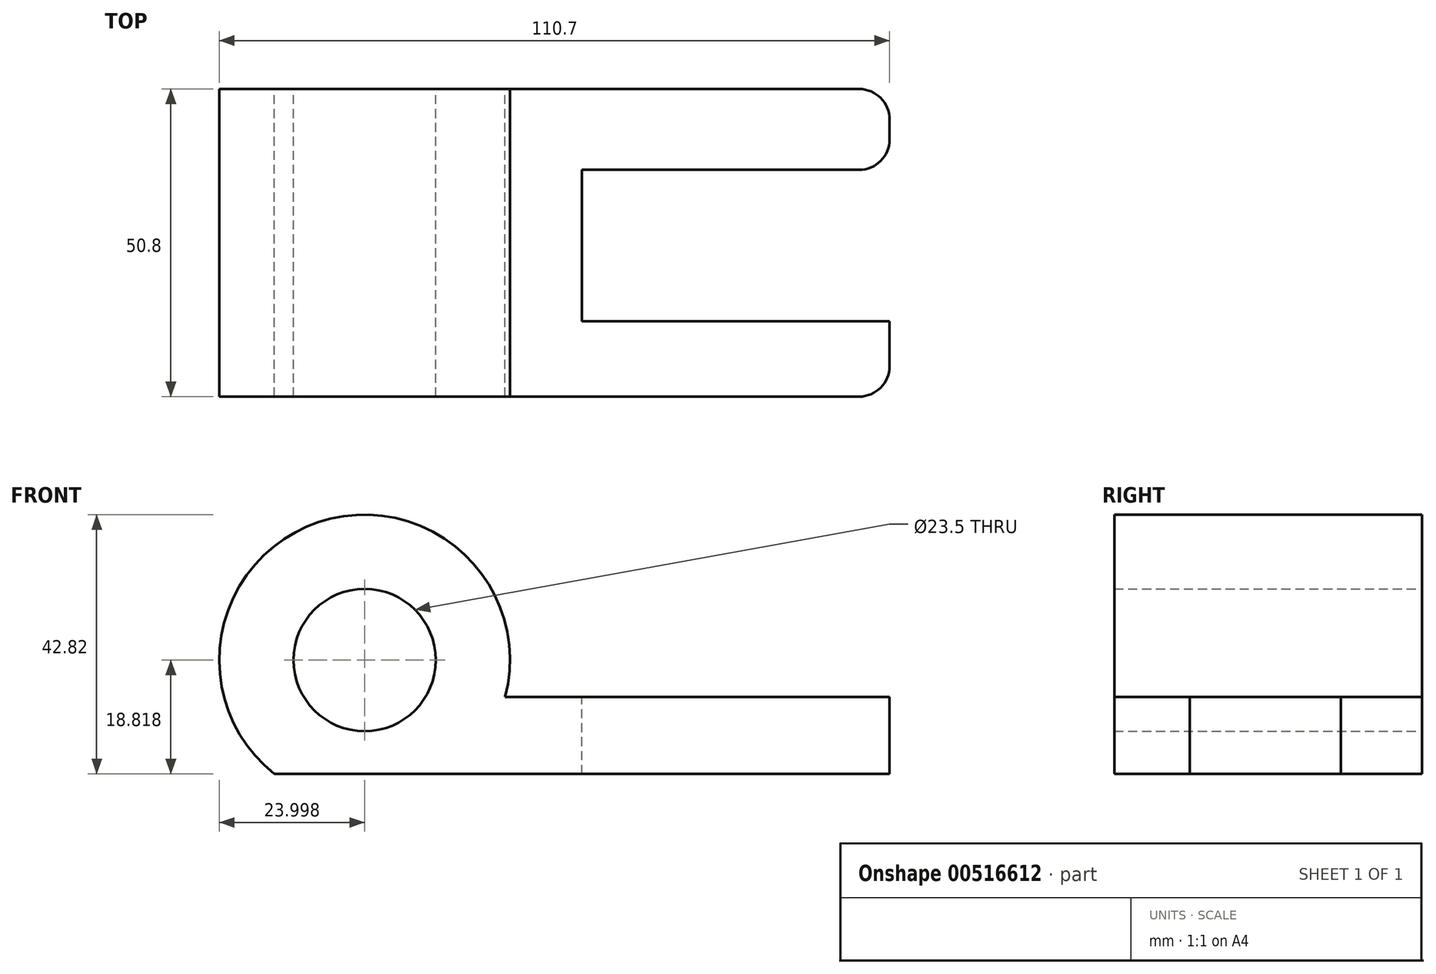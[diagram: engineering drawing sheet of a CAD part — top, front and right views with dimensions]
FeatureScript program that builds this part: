
annotation { "Feature Type Name" : "Feature", "Feature Type Description" : "" }
export const myFeature = defineFeature(function(context is Context, id is Id, definition is map)
    precondition{}
    {
        {
            var Q0;
            Q0=qCreatedBy(makeId("Front.planeOp"),FACE);
            var sketch = newSketch(context, id + "F0", { "sketchPlane" : qUnion([Q0])});
            skLineSegment(sketch, "E0", {"start": v(-60.05, -12.7) * mm, "end": v(41.55, -12.7) * mm});
            skLineSegment(sketch, "E1", {"start": v(41.55, -12.7) * mm, "end": v(41.55, 0) * mm});
            skLineSegment(sketch, "E2", {"start": v(41.55, 0) * mm, "end": v(-21.95, 0) * mm});
            skArc(sketch, "E3", {"start": v(-21.95, 0) * mm, "mid": v(-52.74, 28.89) * mm, "end": v(-60.05, -12.7) * mm});
            skCircle(sketch, "E4", {"center": v(-45.15, 6.12) * mm, "radius": 11.75 * mm});
            skSolve(sketch);
        }
        {
            var Q0;
            Q0=makeQuery(id+"F0.imprint","IMPRINT",FACE,{"disambiguationData":[TD([[makeQuery(id+"F0.imprint","IMPRINT",EDGE,{"derivedFrom":sQuery(id+"F0.wireOp",EDGE,"E0")}),1.0]])]});
            extrude(context, id + "F1", {"entities" : qUnion([Q0]), "depth" : 25.4 * mm, "offsetDistance" : 25.4 * mm});
        }
        {
            var Q0;
            Q0=makeQuery(id+"F1.opExtrude","CAP_FACE",FACE,{"disambiguationData":[OSD([sQuery(id+"F0.wireOp",EDGE,"E0"),sQuery(id+"F0.wireOp",EDGE,"E1"),sQuery(id+"F0.wireOp",EDGE,"E2"),sQuery(id+"F0.wireOp",EDGE,"E3"),sQuery(id+"F0.wireOp",EDGE,"E4")])],"isStart":true});
            extrude(context, id + "F2", {"entities" : qUnion([Q0]), "operationType" : NewBodyOperationType.ADD, "depth" : 25.4 * mm, "offsetDistance" : 25.4 * mm});
        }
        {
            var Q0;
            {var subQ0=sQuery(id+"F0.wireOp",EDGE,"E2");Q0=makeQuery(id+"F2.boolean.opBoolean","MERGE",FACE,{"derivedFrom":[makeQuery(id+"F1.opExtrude","SWEPT_FACE",FACE,{"disambiguationData":[OSD([subQ0])]}),makeQuery(id+"F2.opExtrude","SWEPT_FACE",FACE,{"disambiguationData":[OSD([subQ0])]})]});}
            var sketch = newSketch(context, id + "F3", { "sketchPlane" : qUnion([Q0])});
            skLineSegment(sketch, "E5", {"start": v(41.55, 12.03) * mm, "end": v(-9.25, 12.03) * mm});
            skLineSegment(sketch, "E6", {"start": v(41.55, -12.96) * mm, "end": v(-9.25, -12.96) * mm});
            skLineSegment(sketch, "E7", {"start": v(-9.25, -12.96) * mm, "end": v(-9.25, 12.03) * mm});
            skSolve(sketch);
        }
        {
            var Q0;
            {var subQ0=sQuery(id+"F3.wireOp",EDGE,"E5");Q0=makeQuery(id+"F3.imprint","IMPRINT",FACE,{"disambiguationData":[TD([[makeQuery(id+"F3.imprint","IMPRINT",EDGE,{"derivedFrom":subQ0}),1.0]])]});}
            extrude(context, id + "F4", {"entities" : qUnion([Q0]), "operationType" : NewBodyOperationType.REMOVE, "oppositeDirection" : true, "depth" : 25.4 * mm, "offsetDistance" : 25.4 * mm});
        }
        {
            var Q0;
            Q0=makeQuery(id+"F4.boolean.opBoolean","COPY",EDGE,{"derivedFrom":makeQuery(id+"F4.opExtrude","SWEPT_EDGE",EDGE,{"disambiguationData":[OSD([sQuery(id+"F0.wireOp",EDGE,"E1"),sQuery(id+"F0.wireOp",EDGE,"E2"),sQuery(id+"F3.wireOp",EDGE,"E5")])]})});
            var Q1;
            Q1=makeQuery(id+"F2.opExtrude","CAP_EDGE",EDGE,{"disambiguationData":[OSD([sQuery(id+"F0.wireOp",EDGE,"E1")])],"isStart":false});
            fillet(context, id + "F5", {"entities" : qUnion([Q0, Q1]), "radius" : 5.08 * mm, "tangentPropagation" : true, "allowEdgeOverflow" : false});
        }
        {
            var Q0;
            Q0=makeQuery(id+"F4.boolean.opBoolean","COPY",EDGE,{"derivedFrom":makeQuery(id+"F4.opExtrude","SWEPT_EDGE",EDGE,{"disambiguationData":[OSD([sQuery(id+"F0.wireOp",EDGE,"E1"),sQuery(id+"F0.wireOp",EDGE,"E2"),sQuery(id+"F3.wireOp",EDGE,"E6")])]})});
            var Q1;
            Q1=makeQuery(id+"F1.opExtrude","CAP_EDGE",EDGE,{"disambiguationData":[OSD([sQuery(id+"F0.wireOp",EDGE,"E1")])],"isStart":false});
            fillet(context, id + "F6", {"entities" : qUnion([Q0, Q1]), "radius" : 5.08 * mm, "tangentPropagation" : true, "allowEdgeOverflow" : false});
        }
    });
